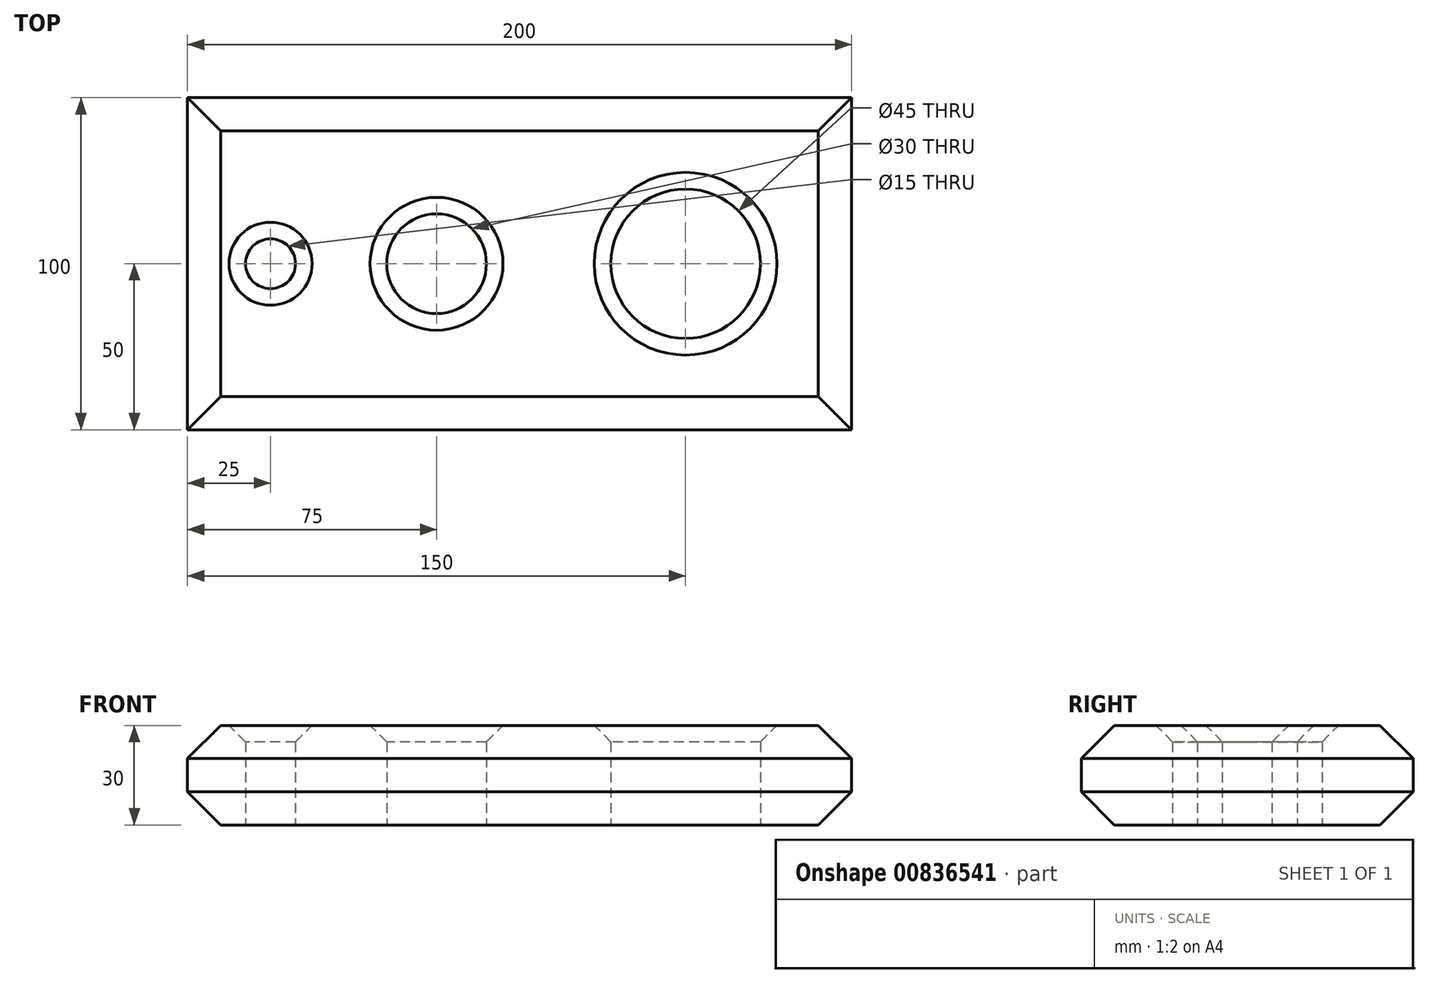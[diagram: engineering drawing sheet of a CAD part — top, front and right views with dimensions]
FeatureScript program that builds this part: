
annotation { "Feature Type Name" : "Feature", "Feature Type Description" : "" }
export const myFeature = defineFeature(function(context is Context, id is Id, definition is map)
    precondition{}
    {
        {
            var Q0;
            Q0=qCreatedBy(makeId("Top.planeOp"),FACE);
            var sketch = newSketch(context, id + "F0", { "sketchPlane" : qUnion([Q0])});
            skLineSegment(sketch, "E0.bottom", {"start": v(0, 0) * mm, "end": v(-200, 0) * mm});
            skLineSegment(sketch, "E0.top", {"start": v(0, 100) * mm, "end": v(-200, 100) * mm});
            skLineSegment(sketch, "E0.left", {"start": v(0, 0) * mm, "end": v(0, 100) * mm});
            skLineSegment(sketch, "E0.right", {"start": v(-200, 0) * mm, "end": v(-200, 100) * mm});
            skCircle(sketch, "E1", {"center": v(-50, 50) * mm, "radius": 22.5 * mm});
            skCircle(sketch, "E2", {"center": v(-125, 50) * mm, "radius": 15 * mm});
            skCircle(sketch, "E3", {"center": v(-175, 50) * mm, "radius": 7.5 * mm});
            skLineSegment(sketch, "E4", {"start": v(-200, 50) * mm, "end": v(0, 50) * mm, "construction": true});
            skSolve(sketch);
        }
        {
            var Q0;
            Q0 = qSketchRegion(id + "F0", true);
            extrude(context, id + "F1", {"entities" : qUnion([Q0]), "depth" : 30 * mm, "offsetDistance" : 25 * mm});
        }
        {
            var Q0;
            Q0=makeQuery(id+"F1.opExtrude","CAP_EDGE",EDGE,{"disambiguationData":[OSD([sQuery(id+"F0.wireOp",EDGE,"E0.right")])],"isStart":false});
            var Q1;
            Q1=makeQuery(id+"F1.opExtrude","CAP_EDGE",EDGE,{"disambiguationData":[OSD([sQuery(id+"F0.wireOp",EDGE,"E0.right")])],"isStart":true});
            var Q2;
            Q2=makeQuery(id+"F1.opExtrude","CAP_EDGE",EDGE,{"disambiguationData":[OSD([sQuery(id+"F0.wireOp",EDGE,"E0.top")])],"isStart":true});
            var Q3;
            Q3=makeQuery(id+"F1.opExtrude","CAP_EDGE",EDGE,{"disambiguationData":[OSD([sQuery(id+"F0.wireOp",EDGE,"E0.top")])],"isStart":false});
            var Q4;
            Q4=makeQuery(id+"F1.opExtrude","CAP_EDGE",EDGE,{"disambiguationData":[OSD([sQuery(id+"F0.wireOp",EDGE,"E0.bottom")])],"isStart":true});
            var Q5;
            Q5=makeQuery(id+"F1.opExtrude","CAP_EDGE",EDGE,{"disambiguationData":[OSD([sQuery(id+"F0.wireOp",EDGE,"E0.bottom")])],"isStart":false});
            var Q6;
            Q6=makeQuery(id+"F1.opExtrude","CAP_EDGE",EDGE,{"disambiguationData":[OSD([sQuery(id+"F0.wireOp",EDGE,"E0.left")])],"isStart":false});
            var Q7;
            Q7=makeQuery(id+"F1.opExtrude","CAP_EDGE",EDGE,{"disambiguationData":[OSD([sQuery(id+"F0.wireOp",EDGE,"E0.left")])],"isStart":true});
            chamfer(context, id + "F2", {"entities" : qUnion([Q0, Q1, Q2, Q3, Q4, Q5, Q6, Q7]), "width" : 10 * mm, "tangentPropagation" : true});
        }
        {
            var Q0;
            Q0=makeQuery(id+"F1.opExtrude","CAP_EDGE",EDGE,{"disambiguationData":[OSD([sQuery(id+"F0.wireOp",EDGE,"E2")])],"isStart":false});
            var Q1;
            Q1=makeQuery(id+"F1.opExtrude","CAP_EDGE",EDGE,{"disambiguationData":[OSD([sQuery(id+"F0.wireOp",EDGE,"E3")])],"isStart":false});
            var Q2;
            Q2=makeQuery(id+"F1.opExtrude","CAP_EDGE",EDGE,{"disambiguationData":[OSD([sQuery(id+"F0.wireOp",EDGE,"E1")])],"isStart":false});
            chamfer(context, id + "F3", {"entities" : qUnion([Q0, Q1, Q2]), "width" : 5 * mm, "tangentPropagation" : true});
        }
    });
